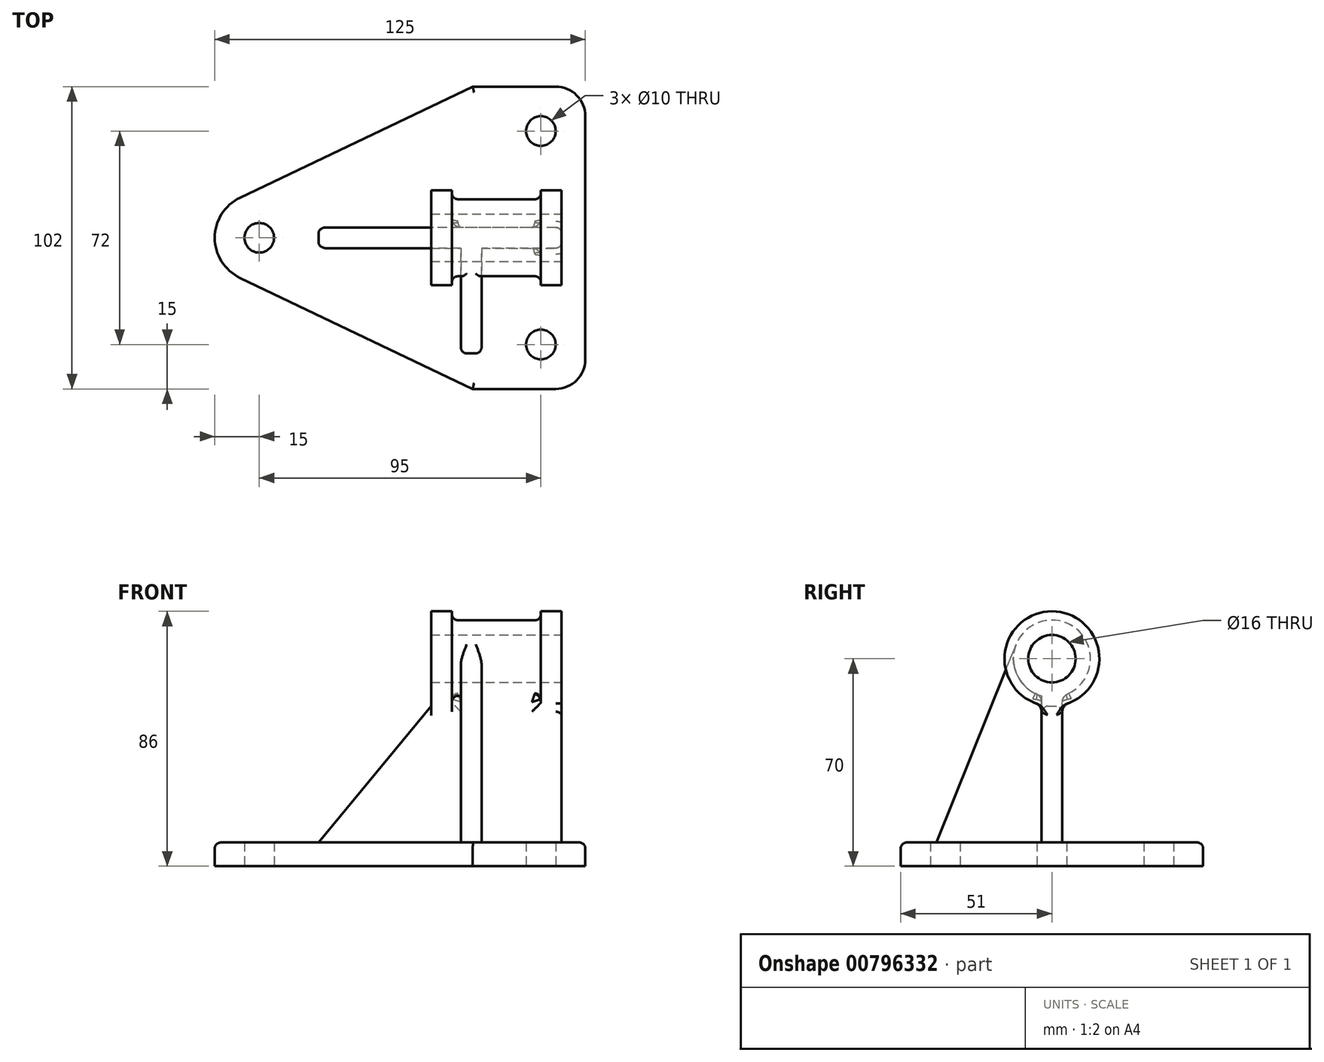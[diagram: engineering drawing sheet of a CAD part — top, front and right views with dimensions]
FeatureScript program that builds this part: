
annotation { "Feature Type Name" : "Feature", "Feature Type Description" : "" }
export const myFeature = defineFeature(function(context is Context, id is Id, definition is map)
    precondition{}
    {
        {
            var Q0;
            Q0=qCreatedBy(makeId("Top.planeOp"),FACE);
            var sketch = newSketch(context, id + "F0", { "sketchPlane" : qUnion([Q0])});
            skCircle(sketch, "E0", {"center": v(0, 0) * mm, "radius": 5 * mm});
            skLineSegment(sketch, "E1", {"start": v(0, 0) * mm, "end": v(110, 0) * mm, "construction": true});
            skArc(sketch, "E2", {"start": v(-6.46, 13.54) * mm, "mid": v(-15, 0) * mm, "end": v(-6.46, -13.54) * mm});
            skLineSegment(sketch, "E3", {"start": v(110, 0) * mm, "end": v(110, 41) * mm});
            skLineSegment(sketch, "E4", {"start": v(100, 51) * mm, "end": v(72, 51) * mm});
            skLineSegment(sketch, "E5", {"start": v(72, 51) * mm, "end": v(-6.46, 13.54) * mm});
            skPoint(sketch, "E6.visualSharp", {"position": v(110, 51) * mm});
            skArc(sketch, "E6.filletArc", {"start": v(110, 41) * mm, "mid": v(107.07, 48.07) * mm, "end": v(100, 51) * mm});
            skCircle(sketch, "E7", {"center": v(95, 36) * mm, "radius": 5 * mm});
            skLineSegment(sketch, "E8.MirrorCS", {"start": v(110, 0) * mm, "end": v(110, -41) * mm});
            skArc(sketch, "E9.MirrorCS", {"start": v(110, -41) * mm, "mid": v(107.07, -48.07) * mm, "end": v(100, -51) * mm});
            skCircle(sketch, "E10.MirrorC", {"center": v(95, -36) * mm, "radius": 5 * mm});
            skLineSegment(sketch, "E11.MirrorCS", {"start": v(100, -51) * mm, "end": v(72, -51) * mm});
            skLineSegment(sketch, "E12.MirrorCS", {"start": v(72, -51) * mm, "end": v(-6.46, -13.54) * mm});
            skSolve(sketch);
        }
        {
            var Q0;
            Q0 = qSketchRegion(id + "F0", true);
            extrude(context, id + "F1", {"entities" : qUnion([Q0]), "depth" : 8 * mm, "offsetDistance" : 25 * mm});
        }
        {
            var Q0;
            Q0=qCreatedBy(makeId("Front.planeOp"),FACE);
            var sketch = newSketch(context, id + "F2", { "sketchPlane" : qUnion([Q0])});
            skLineSegment(sketch, "E13", {"start": v(107.38, 70) * mm, "end": v(45.36, 70) * mm, "construction": true});
            skLineSegment(sketch, "E14", {"start": v(58, 78) * mm, "end": v(58, 86) * mm});
            skLineSegment(sketch, "E15", {"start": v(58, 86) * mm, "end": v(65, 86) * mm});
            skLineSegment(sketch, "E16", {"start": v(65, 86) * mm, "end": v(65, 83) * mm});
            skLineSegment(sketch, "E17", {"start": v(65, 83) * mm, "end": v(95, 83) * mm});
            skLineSegment(sketch, "E18", {"start": v(95, 83) * mm, "end": v(95, 86) * mm});
            skLineSegment(sketch, "E19", {"start": v(95, 86) * mm, "end": v(102, 86) * mm});
            skLineSegment(sketch, "E20", {"start": v(102, 86) * mm, "end": v(102, 78) * mm});
            skLineSegment(sketch, "E21", {"start": v(102, 78) * mm, "end": v(58, 78) * mm});
            skSolve(sketch);
        }
        {
            var Q0;
            Q0=makeQuery(id+"F2.imprint","IMPRINT",FACE,{"disambiguationData":[TD([[makeQuery(id+"F2.imprint","IMPRINT",EDGE,{"derivedFrom":sQuery(id+"F2.wireOp",EDGE,"E14")}),-1.0]])]});
            var Q1;
            Q1=sQuery(id+"F2.wireOp",EDGE,"E13");
            revolve(context, id + "F3", {"surfaceOperationType" : NewSurfaceOperationType.NEW, "entities" : qUnion([Q0]), "axis" : qUnion([Q1]), "revolveType" : RevolveType.FULL});
        }
        {
            var Q0;
            Q0=qCreatedBy(makeId("Front.planeOp"),FACE);
            var sketch = newSketch(context, id + "F4", { "sketchPlane" : qUnion([Q0])});
            skLineSegment(sketch, "E22.0", {"start": v(110, 8) * mm, "end": v(100, 8) * mm});
            skLineSegment(sketch, "E23.0", {"start": v(100, 8) * mm, "end": v(72, 8) * mm});
            skLineSegment(sketch, "E24.0", {"start": v(72, 8) * mm, "end": v(-6.46, 8) * mm});
            skLineSegment(sketch, "E25.0", {"start": v(102, 86) * mm, "end": v(102, 54) * mm});
            skLineSegment(sketch, "E26.0", {"start": v(58, 86) * mm, "end": v(58, 54) * mm});
            skLineSegment(sketch, "E27", {"start": v(58, 54) * mm, "end": v(20, 8) * mm});
            skLineSegment(sketch, "E28", {"start": v(102, 54) * mm, "end": v(102, 8) * mm});
            skLineSegment(sketch, "E29", {"start": v(58, 60) * mm, "end": v(102, 60) * mm});
            skSolve(sketch);
        }
        {
            var Q0;
            Q0 = qSketchRegion(id + "F4", true);
            extrude(context, id + "F5", {"entities" : qUnion([Q0]), "operationType" : NewBodyOperationType.ADD, "depth" : 7 * mm, "offsetDistance" : 25 * mm, "symmetric" : true});
        }
        {
            var Q0;
            Q0=makeQuery(id+"F1.opExtrude","SWEPT_FACE",FACE,{"disambiguationData":[OSD([sQuery(id+"F0.wireOp",EDGE,"E3"),sQuery(id+"F0.wireOp",EDGE,"E8.MirrorCS")])]});
            cPlane(context, id + "F6", {"entities" : qUnion([Q0]), "cplaneType" : CPlaneType.OFFSET, "offset" : 35 * mm, "oppositeDirection" : true, "width" : 150 * mm, "height" : 150 * mm});
        }
        {
            var Q0;
            Q0=qCreatedBy(id+"F6.planeOp",FACE);
            var sketch = newSketch(context, id + "F7", { "sketchPlane" : qUnion([Q0])});
            skArc(sketch, "E30.0.0", {"start": v(3.5, 57.48) * mm, "mid": v(0, 83) * mm, "end": v(-3.5, 57.48) * mm});
            skArc(sketch, "E30.0.2", {"start": v(-3.5, 57.48) * mm, "mid": v(0, 83) * mm, "end": v(3.5, 57.48) * mm});
            skLineSegment(sketch, "E31.0", {"start": v(-3.5, 54.39) * mm, "end": v(-3.5, 8) * mm});
            skLineSegment(sketch, "E32", {"start": v(-3.5, 54.39) * mm, "end": v(-3.5, 57.48) * mm});
            skLineSegment(sketch, "E33.0", {"start": v(41, 8) * mm, "end": v(-41, 8) * mm});
            skLineSegment(sketch, "E34", {"start": v(-39, 8) * mm, "end": v(-12.06, 74.86) * mm});
            skSolve(sketch);
        }
        {
            var Q0;
            Q0 = qSketchRegion(id + "F7", true);
            extrude(context, id + "F8", {"entities" : qUnion([Q0]), "operationType" : NewBodyOperationType.ADD, "oppositeDirection" : true, "depth" : 7 * mm, "offsetDistance" : 25 * mm});
        }
        {
            var Q0;
            Q0=makeQuery(id+"F3.opRevolve","SWEPT_EDGE",EDGE,{"disambiguationData":[OSD([sQuery(id+"F2.wireOp",EDGE,"E17"),sQuery(id+"F2.wireOp",EDGE,"E18")])]});
            var Q1;
            Q1=makeQuery(id+"F3.opRevolve","SWEPT_EDGE",EDGE,{"disambiguationData":[OSD([sQuery(id+"F2.wireOp",EDGE,"E16"),sQuery(id+"F2.wireOp",EDGE,"E17")])]});
            var Q2;
            Q2=makeQuery(id+"F8.opExtrude","CAP_EDGE",EDGE,{"disambiguationData":[OSD([sQuery(id+"F7.wireOp",EDGE,"E34")])],"isStart":false});
            var Q3;
            Q3=makeQuery(id+"F8.opExtrude","CAP_EDGE",EDGE,{"disambiguationData":[OSD([sQuery(id+"F7.wireOp",EDGE,"E34")])],"isStart":true});
            var Q4;
            Q4=makeQuery(id+"F5.opExtrude","CAP_EDGE",EDGE,{"disambiguationData":[OSD([sQuery(id+"F4.wireOp",EDGE,"E27")])],"isStart":false});
            var Q5;
            Q5=makeQuery(id+"F5.opExtrude","CAP_EDGE",EDGE,{"disambiguationData":[OSD([sQuery(id+"F4.wireOp",EDGE,"E27")])],"isStart":true});
            var Q6;
            Q6=makeQuery(id+"F5.opExtrude","CAP_EDGE",EDGE,{"disambiguationData":[OSD([sQuery(id+"F4.wireOp",EDGE,"E25.0"),sQuery(id+"F4.wireOp",EDGE,"E28")])],"isStart":false});
            var Q7;
            Q7=makeQuery(id+"F5.opExtrude","CAP_EDGE",EDGE,{"disambiguationData":[OSD([sQuery(id+"F4.wireOp",EDGE,"E25.0"),sQuery(id+"F4.wireOp",EDGE,"E28")])],"isStart":true});
            var Q8;
            Q8=makeQuery(id+"Fn9WFe37exKPLL9_1.1.F8.opExtrude","CAP_EDGE",EDGE,{"disambiguationData":[OSD([sQuery(id+"F7.wireOp",EDGE,"E34")])],"isStart":true});
            var Q9;
            Q9=makeQuery(id+"Fn9WFe37exKPLL9_1.1.F8.opExtrude","CAP_EDGE",EDGE,{"disambiguationData":[OSD([sQuery(id+"F7.wireOp",EDGE,"E34")])],"isStart":false});
            var Q10;
            Q10=makeQuery(id+"F1.opExtrude","CAP_EDGE",EDGE,{"disambiguationData":[OSD([sQuery(id+"F0.wireOp",EDGE,"E5")])],"isStart":false});
            var Q11;
            Q11=makeQuery(id+"F1.opExtrude","CAP_EDGE",EDGE,{"disambiguationData":[OSD([sQuery(id+"F0.wireOp",EDGE,"E4")])],"isStart":false});
            fillet(context, id + "F9", {"entities" : qUnion([Q0, Q1, Q2, Q3, Q4, Q5, Q6, Q7, Q8, Q9, Q10, Q11]), "radius" : 2 * mm, "tangentPropagation" : true, "allowEdgeOverflow" : false});
        }
        {
            var Q0;
            Q0=makeQuery(id+"Fn9WFe37exKPLL9_1.1.F8.opExtrude","CAP_EDGE",EDGE,{"disambiguationData":[OSD([sQuery(id+"F7.wireOp",EDGE,"E31.0"),sQuery(id+"F7.wireOp",EDGE,"E32")])],"isStart":true});
            var Q1;
            Q1=makeQuery(id+"F8.opExtrude","CAP_EDGE",EDGE,{"disambiguationData":[OSD([sQuery(id+"F7.wireOp",EDGE,"E31.0"),sQuery(id+"F7.wireOp",EDGE,"E32")])],"isStart":true});
            var Q2;
            Q2=makeQuery(id+"F8.opExtrude","CAP_EDGE",EDGE,{"disambiguationData":[OSD([sQuery(id+"F7.wireOp",EDGE,"E31.0"),sQuery(id+"F7.wireOp",EDGE,"E32")])],"isStart":false});
            var Q3;
            Q3=makeQuery(id+"Fn9WFe37exKPLL9_1.1.F8.opExtrude","CAP_EDGE",EDGE,{"disambiguationData":[OSD([sQuery(id+"F7.wireOp",EDGE,"E31.0"),sQuery(id+"F7.wireOp",EDGE,"E32")])],"isStart":false});
            var Q4;
            {var subQ0=makeQuery(id+"F3.opRevolve","SWEPT_FACE",FACE,{"disambiguationData":[OSD([sQuery(id+"F2.wireOp",EDGE,"E17")])]});var subQ1=makeQuery(id+"F5.opExtrude","CAP_FACE",FACE,{"disambiguationData":[OSD([sQuery(id+"F4.wireOp",EDGE,"E22.0"),sQuery(id+"F4.wireOp",EDGE,"E23.0"),sQuery(id+"F4.wireOp",EDGE,"E24.0"),sQuery(id+"F4.wireOp",EDGE,"E25.0"),sQuery(id+"F4.wireOp",EDGE,"E26.0"),sQuery(id+"F4.wireOp",EDGE,"E27"),sQuery(id+"F4.wireOp",EDGE,"E28"),sQuery(id+"F4.wireOp",EDGE,"E29")])],"isStart":true});Q4=makeQuery(id+"Fn9WFe37exKPLL9_1.1.F8.boolean.opBoolean","SPLIT",EDGE,{"disambiguationData":[TD([makeQuery(id+"F3.opRevolve","SWEPT_FACE",FACE,{"disambiguationData":[OSD([sQuery(id+"F2.wireOp",EDGE,"E18")])]})])],"derivedFrom":makeQuery(id+"F5.boolean.opBoolean","INTERSECT",EDGE,{"derivedFrom":[subQ0,subQ1]})});}
            var Q5;
            Q5=makeQuery(id+"Fn9WFe37exKPLL9_1.1.F8.opExtrude","CAP_EDGE",EDGE,{"disambiguationData":[OSD([sQuery(id+"F7.wireOp",EDGE,"E30.0.2")])],"isStart":true});
            var Q6;
            Q6=makeQuery(id+"Fn9WFe37exKPLL9_1.1.F8.opExtrude","CAP_EDGE",EDGE,{"disambiguationData":[OSD([sQuery(id+"F7.wireOp",EDGE,"E30.0.2")])],"isStart":false});
            var Q7;
            {var subQ0=makeQuery(id+"F3.opRevolve","SWEPT_FACE",FACE,{"disambiguationData":[OSD([sQuery(id+"F2.wireOp",EDGE,"E17")])]});var subQ1=makeQuery(id+"F5.opExtrude","CAP_FACE",FACE,{"disambiguationData":[OSD([sQuery(id+"F4.wireOp",EDGE,"E22.0"),sQuery(id+"F4.wireOp",EDGE,"E23.0"),sQuery(id+"F4.wireOp",EDGE,"E24.0"),sQuery(id+"F4.wireOp",EDGE,"E25.0"),sQuery(id+"F4.wireOp",EDGE,"E26.0"),sQuery(id+"F4.wireOp",EDGE,"E27"),sQuery(id+"F4.wireOp",EDGE,"E28"),sQuery(id+"F4.wireOp",EDGE,"E29")])],"isStart":false});Q7=makeQuery(id+"F8.boolean.opBoolean","SPLIT",EDGE,{"disambiguationData":[TD([makeQuery(id+"F3.opRevolve","SWEPT_FACE",FACE,{"disambiguationData":[OSD([sQuery(id+"F2.wireOp",EDGE,"E18")])]})])],"derivedFrom":makeQuery(id+"F5.boolean.opBoolean","INTERSECT",EDGE,{"derivedFrom":[subQ0,subQ1]})});}
            var Q8;
            Q8=makeQuery(id+"F8.opExtrude","CAP_EDGE",EDGE,{"disambiguationData":[OSD([sQuery(id+"F7.wireOp",EDGE,"E30.0.2")])],"isStart":true});
            var Q9;
            Q9=makeQuery(id+"F8.opExtrude","CAP_EDGE",EDGE,{"disambiguationData":[OSD([sQuery(id+"F7.wireOp",EDGE,"E30.0.2")])],"isStart":false});
            var Q10;
            Q10=makeQuery(id+"F5.boolean.opBoolean","INTERSECT",EDGE,{"derivedFrom":[makeQuery(id+"F3.opRevolve","SWEPT_FACE",FACE,{"disambiguationData":[OSD([sQuery(id+"F2.wireOp",EDGE,"E19")])]}),makeQuery(id+"F5.opExtrude","CAP_FACE",FACE,{"disambiguationData":[OSD([sQuery(id+"F4.wireOp",EDGE,"E22.0"),sQuery(id+"F4.wireOp",EDGE,"E23.0"),sQuery(id+"F4.wireOp",EDGE,"E24.0"),sQuery(id+"F4.wireOp",EDGE,"E25.0"),sQuery(id+"F4.wireOp",EDGE,"E26.0"),sQuery(id+"F4.wireOp",EDGE,"E27"),sQuery(id+"F4.wireOp",EDGE,"E28"),sQuery(id+"F4.wireOp",EDGE,"E29")])],"isStart":false})]});
            var Q11;
            Q11=makeQuery(id+"F5.boolean.opBoolean","INTERSECT",EDGE,{"derivedFrom":[makeQuery(id+"F3.opRevolve","SWEPT_FACE",FACE,{"disambiguationData":[OSD([sQuery(id+"F2.wireOp",EDGE,"E19")])]}),makeQuery(id+"F5.opExtrude","CAP_FACE",FACE,{"disambiguationData":[OSD([sQuery(id+"F4.wireOp",EDGE,"E22.0"),sQuery(id+"F4.wireOp",EDGE,"E23.0"),sQuery(id+"F4.wireOp",EDGE,"E24.0"),sQuery(id+"F4.wireOp",EDGE,"E25.0"),sQuery(id+"F4.wireOp",EDGE,"E26.0"),sQuery(id+"F4.wireOp",EDGE,"E27"),sQuery(id+"F4.wireOp",EDGE,"E28"),sQuery(id+"F4.wireOp",EDGE,"E29")])],"isStart":true})]});
            fillet(context, id + "F10", {"entities" : qUnion([Q0, Q1, Q2, Q3, Q4, Q5, Q6, Q7, Q8, Q9, Q10, Q11]), "radius" : 3 * mm, "tangentPropagation" : true, "allowEdgeOverflow" : false});
        }
        {
            var Q0;
            Q0=makeQuery(id+"Fn9WFe37exKPLL9_1.1.F8.opExtrude","CAP_EDGE",EDGE,{"disambiguationData":[OSD([sQuery(id+"F7.wireOp",EDGE,"E33.0")])],"isStart":true});
            var Q1;
            Q1=makeQuery(id+"F5.boolean.opBoolean","INTERSECT",EDGE,{"derivedFrom":[makeQuery(id+"F3.opRevolve","SWEPT_FACE",FACE,{"disambiguationData":[OSD([sQuery(id+"F2.wireOp",EDGE,"E15")])]}),makeQuery(id+"F5.opExtrude","CAP_FACE",FACE,{"disambiguationData":[OSD([sQuery(id+"F4.wireOp",EDGE,"E22.0"),sQuery(id+"F4.wireOp",EDGE,"E23.0"),sQuery(id+"F4.wireOp",EDGE,"E24.0"),sQuery(id+"F4.wireOp",EDGE,"E25.0"),sQuery(id+"F4.wireOp",EDGE,"E26.0"),sQuery(id+"F4.wireOp",EDGE,"E27"),sQuery(id+"F4.wireOp",EDGE,"E28"),sQuery(id+"F4.wireOp",EDGE,"E29")])],"isStart":true})]});
            var Q2;
            Q2=makeQuery(id+"F5.boolean.opBoolean","INTERSECT",EDGE,{"derivedFrom":[makeQuery(id+"F3.opRevolve","SWEPT_FACE",FACE,{"disambiguationData":[OSD([sQuery(id+"F2.wireOp",EDGE,"E15")])]}),makeQuery(id+"F5.opExtrude","CAP_FACE",FACE,{"disambiguationData":[OSD([sQuery(id+"F4.wireOp",EDGE,"E22.0"),sQuery(id+"F4.wireOp",EDGE,"E23.0"),sQuery(id+"F4.wireOp",EDGE,"E24.0"),sQuery(id+"F4.wireOp",EDGE,"E25.0"),sQuery(id+"F4.wireOp",EDGE,"E26.0"),sQuery(id+"F4.wireOp",EDGE,"E27"),sQuery(id+"F4.wireOp",EDGE,"E28"),sQuery(id+"F4.wireOp",EDGE,"E29")])],"isStart":false})]});
            fillet(context, id + "F11", {"entities" : qUnion([Q0, Q1, Q2]), "radius" : 3 * mm, "tangentPropagation" : true, "allowEdgeOverflow" : false});
        }
    });
